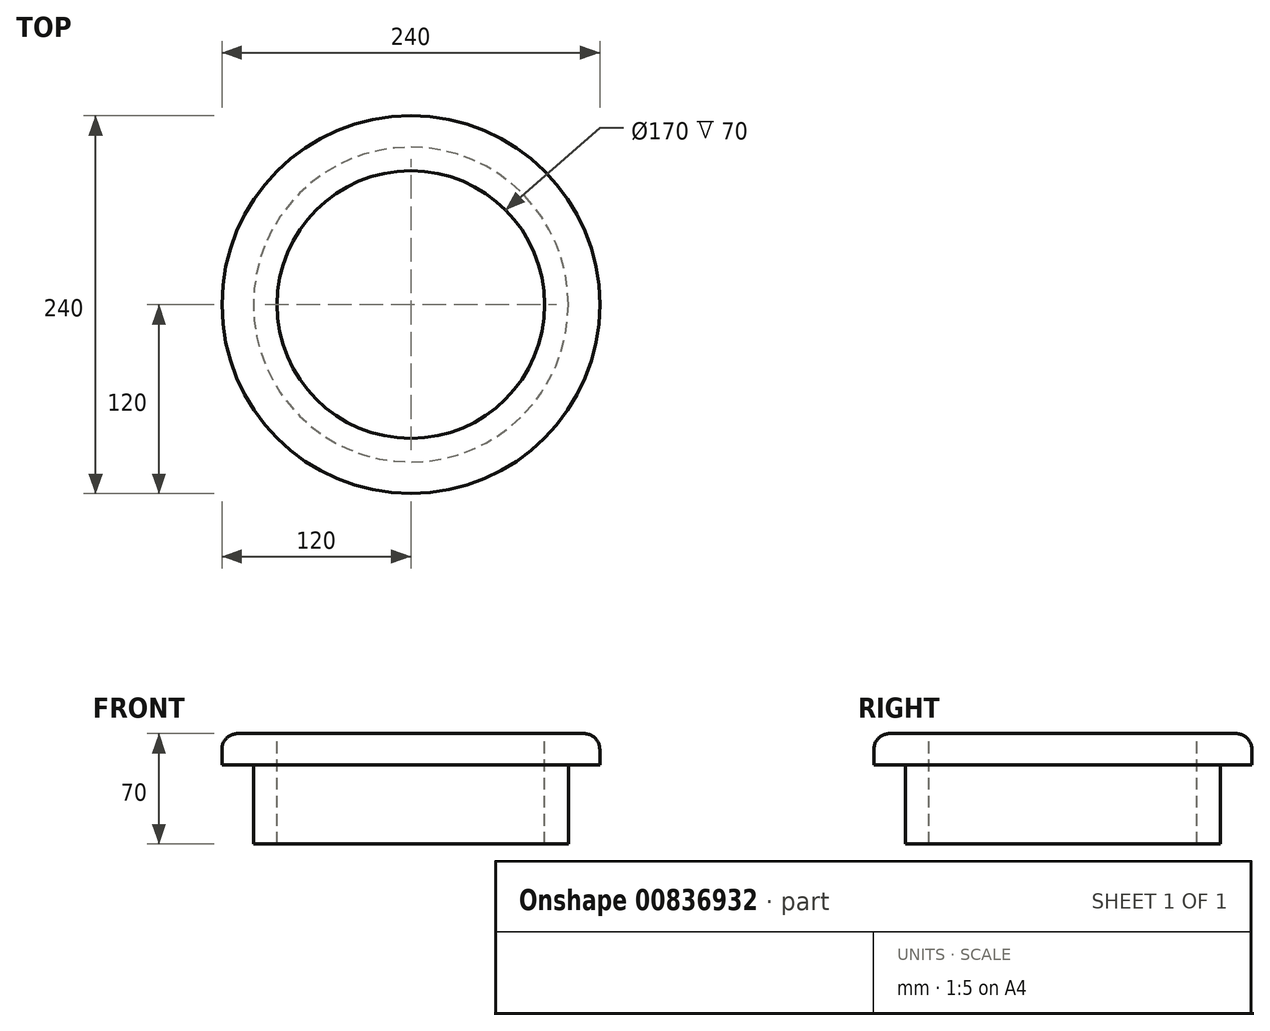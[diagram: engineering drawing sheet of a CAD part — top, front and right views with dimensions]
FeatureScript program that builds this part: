
annotation { "Feature Type Name" : "Feature", "Feature Type Description" : "" }
export const myFeature = defineFeature(function(context is Context, id is Id, definition is map)
    precondition{}
    {
        {
            var Q0;
            Q0=qCreatedBy(makeId("Top.planeOp"),FACE);
            var sketch = newSketch(context, id + "F0", { "sketchPlane" : qUnion([Q0])});
            skCircle(sketch, "E0", {"center": v(0, 0) * mm, "radius": 100 * mm});
            skCircle(sketch, "E1", {"center": v(0, 0) * mm, "radius": 120 * mm});
            skCircle(sketch, "E2", {"center": v(0, 0) * mm, "radius": 85 * mm});
            skSolve(sketch);
        }
        {
            var Q0;
            Q0=makeQuery(id+"F0.imprint","IMPRINT",FACE,{"disambiguationData":[TD([[makeQuery(id+"F0.imprint","IMPRINT",EDGE,{"derivedFrom":sQuery(id+"F0.wireOp",EDGE,"E0")}),1.0]])]});
            extrude(context, id + "F1", {"entities" : qUnion([Q0]), "oppositeDirection" : true, "depth" : 50 * mm, "offsetDistance" : 25 * mm});
        }
        {
            var Q0;
            Q0 = qSketchRegion(id + "F0", true);
            var Q1;
            Q1=makeQuery(id+"F0.imprint","IMPRINT",FACE,{"disambiguationData":[TD([[makeQuery(id+"F0.imprint","IMPRINT",EDGE,{"derivedFrom":sQuery(id+"F0.wireOp",EDGE,"E0")}),1.0]])]});
            extrude(context, id + "F2", {"entities" : qUnion([Q0, Q1]), "operationType" : NewBodyOperationType.ADD, "depth" : 20 * mm, "offsetDistance" : 25 * mm});
        }
        {
            var Q0;
            Q0=makeQuery(id+"F2.opExtrude","CAP_EDGE",EDGE,{"disambiguationData":[OSD([sQuery(id+"F0.wireOp",EDGE,"E1")])],"isStart":false});
            fillet(context, id + "F3", {"entities" : qUnion([Q0]), "radius" : 10 * mm, "tangentPropagation" : true, "allowEdgeOverflow" : false});
        }
    });
